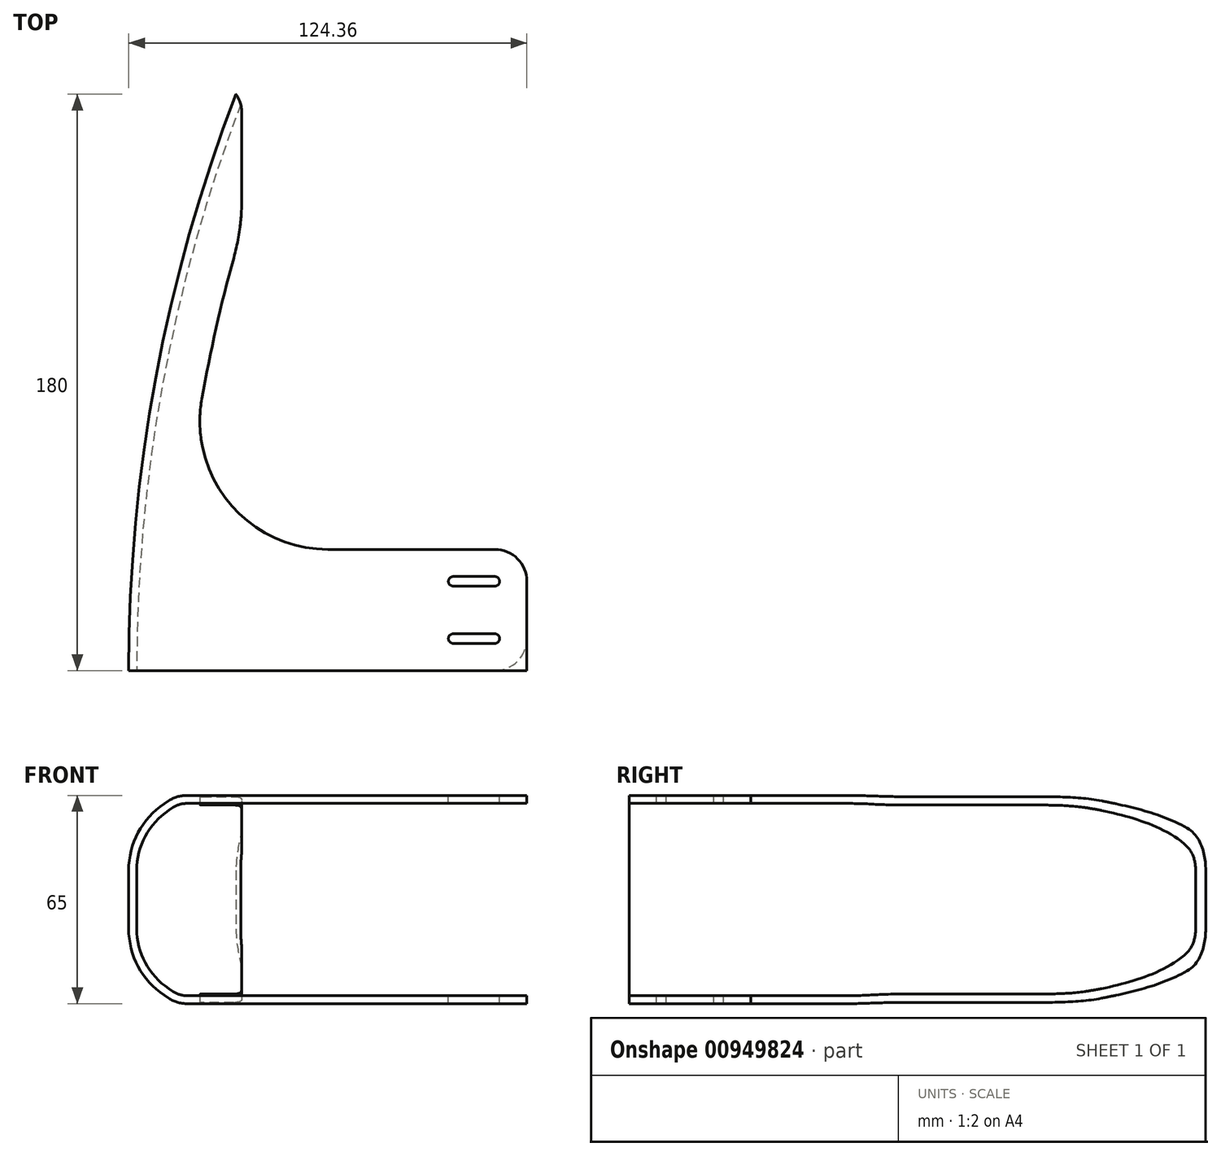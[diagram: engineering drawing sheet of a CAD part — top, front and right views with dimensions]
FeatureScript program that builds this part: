
annotation { "Feature Type Name" : "Feature", "Feature Type Description" : "" }
export const myFeature = defineFeature(function(context is Context, id is Id, definition is map)
    precondition{}
    {
        {
            var Q0;
            Q0=qCreatedBy(makeId("Top.planeOp"),FACE);
            var sketch = newSketch(context, id + "F0", { "sketchPlane" : qUnion([Q0])});
            skArc(sketch, "E0", {"start": v(-500, 0) * mm, "mid": v(-491.55, 91.55) * mm, "end": v(-466.48, 180) * mm});
            skLineSegment(sketch, "E1", {"start": v(-466.48, 180) * mm, "end": v(0, 0) * mm});
            skLineSegment(sketch, "E2", {"start": v(-500, 0) * mm, "end": v(0, 0) * mm});
            skSolve(sketch);
        }
        {
            var Q0;
            Q0=qSketchRegion(id+"F0",true);
            extrude(context, id + "F1", {"entities" : qUnion([Q0]), "depth" : 65 * mm, "offsetDistance" : 25 * mm});
        }
        {
            var Q0;
            Q0=makeQuery(id+"F1.opExtrude","CAP_EDGE",EDGE,{"disambiguationData":[OSD([sQuery(id+"F0.wireOp",EDGE,"E0")])],"isStart":true});
            var Q1;
            Q1=makeQuery(id+"F1.opExtrude","CAP_EDGE",EDGE,{"disambiguationData":[OSD([sQuery(id+"F0.wireOp",EDGE,"E0")])],"isStart":false});
            chamfer(context, id + "F2", {"entities" : qUnion([Q0, Q1]), "chamferType" : ChamferType.TWO_OFFSETS, "width1" : 10 * mm, "oppositeDirection" : false, "width2" : 15 * mm, "tangentPropagation" : true});
        }
        {
            var Q0;
            {var subQ0=sQuery(id+"F0.wireOp",EDGE,"E0");Q0=makeQuery(id+"F2.opChamfer","BLEND_EDGE",EDGE,{"blendedFrom":[makeQuery(id+"F1.opExtrude","CAP_EDGE",EDGE,{"disambiguationData":[OSD([subQ0])],"isStart":false}),makeQuery(id+"F1.opExtrude","SWEPT_FACE",FACE,{"disambiguationData":[OSD([subQ0])]})],"blendedInto":[makeQuery(id+"F1.opExtrude","SWEPT_FACE",FACE,{"disambiguationData":[OSD([subQ0])]})]});}
            var Q1;
            {var subQ0=sQuery(id+"F0.wireOp",EDGE,"E0");Q1=makeQuery(id+"F2.opChamfer","BLEND_EDGE",EDGE,{"blendedFrom":[makeQuery(id+"F1.opExtrude","CAP_EDGE",EDGE,{"disambiguationData":[OSD([subQ0])],"isStart":true}),makeQuery(id+"F1.opExtrude","SWEPT_FACE",FACE,{"disambiguationData":[OSD([subQ0])]})],"blendedInto":[makeQuery(id+"F1.opExtrude","SWEPT_FACE",FACE,{"disambiguationData":[OSD([subQ0])]})]});}
            fillet(context, id + "F3", {"entities" : qUnion([Q0, Q1]), "radius" : 25 * mm, "tangentPropagation" : true, "allowEdgeOverflow" : false});
        }
        {
            var Q0;
            {var subQ0=sQuery(id+"F0.wireOp",EDGE,"E0");Q0=makeQuery(id+"F2.opChamfer","BLEND_EDGE",EDGE,{"blendedFrom":[makeQuery(id+"F1.opExtrude","CAP_EDGE",EDGE,{"disambiguationData":[OSD([subQ0])],"isStart":false}),makeQuery(id+"F1.opExtrude","CAP_FACE",FACE,{"disambiguationData":[OSD([subQ0,sQuery(id+"F0.wireOp",EDGE,"E1"),sQuery(id+"F0.wireOp",EDGE,"E2")])],"isStart":false})],"blendedInto":[makeQuery(id+"F1.opExtrude","CAP_FACE",FACE,{"disambiguationData":[OSD([subQ0,sQuery(id+"F0.wireOp",EDGE,"E1"),sQuery(id+"F0.wireOp",EDGE,"E2")])],"isStart":false})]});}
            var Q1;
            {var subQ0=sQuery(id+"F0.wireOp",EDGE,"E0");Q1=makeQuery(id+"F2.opChamfer","BLEND_EDGE",EDGE,{"blendedFrom":[makeQuery(id+"F1.opExtrude","CAP_EDGE",EDGE,{"disambiguationData":[OSD([subQ0])],"isStart":true}),makeQuery(id+"F1.opExtrude","CAP_FACE",FACE,{"disambiguationData":[OSD([subQ0,sQuery(id+"F0.wireOp",EDGE,"E1"),sQuery(id+"F0.wireOp",EDGE,"E2")])],"isStart":true})],"blendedInto":[makeQuery(id+"F1.opExtrude","CAP_FACE",FACE,{"disambiguationData":[OSD([subQ0,sQuery(id+"F0.wireOp",EDGE,"E1"),sQuery(id+"F0.wireOp",EDGE,"E2")])],"isStart":true})]});}
            fillet(context, id + "F4", {"entities" : qUnion([Q0, Q1]), "radius" : 10 * mm, "tangentPropagation" : true, "allowEdgeOverflow" : false});
        }
        {
            var Q0;
            Q0=makeQuery(id+"F1.opExtrude","CAP_FACE",FACE,{"disambiguationData":[OSD([sQuery(id+"F0.wireOp",EDGE,"E0"),sQuery(id+"F0.wireOp",EDGE,"E1"),sQuery(id+"F0.wireOp",EDGE,"E2")])],"isStart":true});
            var sketch = newSketch(context, id + "F5", { "sketchPlane" : qUnion([Q0])});
            skLineSegment(sketch, "E3", {"start": v(-375.64, 0) * mm, "end": v(-375.64, -37.87) * mm});
            skLineSegment(sketch, "E4", {"start": v(-375.64, -37.87) * mm, "end": v(-445.64, -37.87) * mm});
            skLineSegment(sketch, "E5", {"start": v(-375.64, 0) * mm, "end": v(0, 0) * mm});
            skLineSegment(sketch, "E6", {"start": v(0, 0) * mm, "end": v(-452.15, -174.47) * mm});
            skArc(sketch, "E7", {"start": v(-480.57, -62.77) * mm, "mid": v(-469.7, -119.47) * mm, "end": v(-452.15, -174.47) * mm});
            skLineSegment(sketch, "E8", {"start": v(-452.15, -174.47) * mm, "end": v(0, 0) * mm});
            skArc(sketch, "E9", {"start": v(-480.57, -62.77) * mm, "mid": v(-482.03, -50.34) * mm, "end": v(-483.17, -37.87) * mm});
            skLineSegment(sketch, "E10", {"start": v(-445.64, -37.87) * mm, "end": v(-483.17, -37.87) * mm});
            skSolve(sketch);
        }
        {
            var Q0;
            Q0=qSketchRegion(id+"F5",true);
            extrude(context, id + "F6", {"entities" : qUnion([Q0]), "operationType" : NewBodyOperationType.REMOVE, "oppositeDirection" : true, "depth" : 100 * mm, "offsetDistance" : 25 * mm});
        }
        {
            var Q0;
            Q0=makeQuery(id+"F6.boolean.opBoolean","COPY",FACE,{"derivedFrom":makeQuery(id+"F6.opExtrude","SWEPT_FACE",FACE,{"disambiguationData":[OSD([sQuery(id+"F5.wireOp",EDGE,"q5jWbjDx-kVAx-P1jz-1uz1-IYKBsqEQwRC3")])]})});
            var Q1;
            Q1=makeQuery(id+"F6.boolean.opBoolean","COPY",FACE,{"derivedFrom":makeQuery(id+"F6.opExtrude","SWEPT_FACE",FACE,{"disambiguationData":[OSD([sQuery(id+"F5.wireOp",EDGE,"E4")])]})});
            var Q2;
            Q2=makeQuery(id+"F6.boolean.opBoolean","COPY",FACE,{"derivedFrom":makeQuery(id+"F6.opExtrude","SWEPT_FACE",FACE,{"disambiguationData":[OSD([sQuery(id+"F5.wireOp",EDGE,"2JUCW0xm-JYR1-ufkW-KHsm-7LWGHGezyxtH")])]})});
            var Q3;
            Q3=makeQuery(id+"F6.boolean.opBoolean","COPY",FACE,{"derivedFrom":makeQuery(id+"F6.opExtrude","SWEPT_FACE",FACE,{"disambiguationData":[OSD([sQuery(id+"F5.wireOp",EDGE,"E3")])]})});
            var Q4;
            Q4=makeQuery(id+"F6.boolean.opBoolean","COPY",FACE,{"derivedFrom":makeQuery(id+"F6.opExtrude","SWEPT_FACE",FACE,{"disambiguationData":[OSD([sQuery(id+"F5.wireOp",EDGE,"E7")])]})});
            var Q5;
            Q5=makeQuery(id+"F1.opExtrude","SWEPT_FACE",FACE,{"disambiguationData":[OSD([sQuery(id+"F0.wireOp",EDGE,"E1")])]});
            var Q6;
            Q6=makeQuery(id+"F1.opExtrude","SWEPT_FACE",FACE,{"disambiguationData":[OSD([sQuery(id+"F0.wireOp",EDGE,"E2")])]});
            shell(context, id + "F7", {"entities" : qUnion([Q0, Q1, Q2, Q3, Q4, Q5, Q6]), "thickness" : 2.5 * mm});
        }
        {
            var Q0;
            Q0=makeQuery(id+"F7.opShell","OFFSET_EDGE",EDGE,{"disambiguationData":[OSD([sQuery(id+"F5.wireOp",EDGE,"E3"),sQuery(id+"F5.wireOp",EDGE,"E4")])]});
            var Q1;
            Q1=makeQuery(id+"F7.opShell","OFFSET_EDGE",EDGE,{"disambiguationData":[OSD([sQuery(id+"F0.wireOp",EDGE,"E2"),sQuery(id+"F5.wireOp",EDGE,"E3"),sQuery(id+"F5.wireOp",EDGE,"E5")])]});
            var Q2;
            Q2=makeQuery(id+"F6.boolean.opBoolean","COPY",EDGE,{"derivedFrom":makeQuery(id+"F6.opExtrude","SWEPT_EDGE",EDGE,{"disambiguationData":[OSD([sQuery(id+"F5.wireOp",EDGE,"E3"),sQuery(id+"F5.wireOp",EDGE,"E4")])]})});
            var Q3;
            Q3=makeQuery(id+"F6.boolean.opBoolean","COPY",EDGE,{"derivedFrom":makeQuery(id+"F6.opExtrude","SWEPT_EDGE",EDGE,{"disambiguationData":[OSD([sQuery(id+"F0.wireOp",EDGE,"E2"),sQuery(id+"F5.wireOp",EDGE,"E3"),sQuery(id+"F5.wireOp",EDGE,"E5")])]})});
            fillet(context, id + "F8", {"entities" : qUnion([Q0, Q1, Q2, Q3]), "radius" : 10 * mm, "tangentPropagation" : true, "allowEdgeOverflow" : false});
        }
        {
            var Q0;
            Q0=makeQuery(id+"F1.opExtrude","CAP_FACE",FACE,{"disambiguationData":[OSD([sQuery(id+"F0.wireOp",EDGE,"E0"),sQuery(id+"F0.wireOp",EDGE,"E1"),sQuery(id+"F0.wireOp",EDGE,"E2")])],"isStart":false});
            var sketch = newSketch(context, id + "F9", { "sketchPlane" : qUnion([Q0])});
            skCircle(sketch, "E11", {"center": v(-385.64, 27.87) * mm, "radius": 1.5 * mm});
            skCircle(sketch, "E12", {"center": v(-385.64, 10) * mm, "radius": 1.5 * mm});
            skCircle(sketch, "E13", {"center": v(-398.64, 10) * mm, "radius": 1.5 * mm});
            skCircle(sketch, "E14", {"center": v(-398.64, 27.87) * mm, "radius": 1.5 * mm});
            skLineSegment(sketch, "E15", {"start": v(-398.64, 11.5) * mm, "end": v(-385.64, 11.5) * mm});
            skLineSegment(sketch, "E16", {"start": v(-398.64, 26.37) * mm, "end": v(-385.64, 26.37) * mm});
            skLineSegment(sketch, "E17", {"start": v(-385.64, 29.37) * mm, "end": v(-398.64, 29.37) * mm});
            skLineSegment(sketch, "E18", {"start": v(-398.64, 8.5) * mm, "end": v(-385.64, 8.5) * mm});
            skSolve(sketch);
        }
        {
            var Q0;
            Q0=qSketchRegion(id+"F9",true);
            extrude(context, id + "F10", {"entities" : qUnion([Q0]), "operationType" : NewBodyOperationType.REMOVE, "oppositeDirection" : true, "depth" : 500 * mm, "offsetDistance" : 25 * mm});
        }
        {
            var Q0;
            Q0=makeQuery(id+"F6.boolean.opBoolean","COPY",EDGE,{"derivedFrom":makeQuery(id+"F6.opExtrude","SWEPT_EDGE",EDGE,{"disambiguationData":[OSD([sQuery(id+"F5.wireOp",EDGE,"E9"),sQuery(id+"F5.wireOp",EDGE,"E10")])]})});
            var Q1;
            Q1=makeQuery(id+"F7.opShell","OFFSET_EDGE",EDGE,{"disambiguationData":[OSD([sQuery(id+"F5.wireOp",EDGE,"E9"),sQuery(id+"F5.wireOp",EDGE,"E10")])]});
            fillet(context, id + "F11", {"entities" : qUnion([Q0, Q1]), "radius" : 40 * mm, "tangentPropagation" : true, "allowEdgeOverflow" : false});
        }
        {
            var Q0;
            Q0=makeQuery(id+"F7.opShell","OFFSET_EDGE",EDGE,{"disambiguationData":[OSD([sQuery(id+"F5.wireOp",EDGE,"E7"),sQuery(id+"F5.wireOp",EDGE,"E8")])]});
            var Q1;
            Q1=makeQuery(id+"F6.boolean.opBoolean","COPY",EDGE,{"derivedFrom":makeQuery(id+"F6.opExtrude","SWEPT_EDGE",EDGE,{"disambiguationData":[OSD([sQuery(id+"F5.wireOp",EDGE,"E7"),sQuery(id+"F5.wireOp",EDGE,"E8")])]})});
            chamfer(context, id + "F12", {"entities" : qUnion([Q0, Q1]), "chamferType" : ChamferType.TWO_OFFSETS, "width1" : 15 * mm, "oppositeDirection" : false, "width2" : 40 * mm, "tangentPropagation" : true});
        }
        {
            var Q0;
            Q0=makeQuery(id+"F12.opChamfer","BLEND_EDGE",EDGE,{"blendedFrom":[makeQuery(id+"F7.opShell","OFFSET_EDGE",EDGE,{"disambiguationData":[OSD([sQuery(id+"F5.wireOp",EDGE,"E7"),sQuery(id+"F5.wireOp",EDGE,"E8")])]}),makeQuery(id+"F1.opExtrude","SWEPT_FACE",FACE,{"disambiguationData":[OSD([sQuery(id+"F0.wireOp",EDGE,"E1")])]})],"blendedInto":[makeQuery(id+"F1.opExtrude","SWEPT_FACE",FACE,{"disambiguationData":[OSD([sQuery(id+"F0.wireOp",EDGE,"E1")])]})]});
            fillet(context, id + "F13", {"entities" : qUnion([Q0]), "radius" : 10 * mm, "tangentPropagation" : true, "allowEdgeOverflow" : false});
        }
        {
            var Q0;
            {var subQ0=sQuery(id+"F5.wireOp",EDGE,"E7");Q0=makeQuery(id+"F12.opChamfer","BLEND_EDGE",EDGE,{"blendedFrom":[makeQuery(id+"F6.boolean.opBoolean","COPY",EDGE,{"derivedFrom":makeQuery(id+"F6.opExtrude","SWEPT_EDGE",EDGE,{"disambiguationData":[OSD([subQ0,sQuery(id+"F5.wireOp",EDGE,"E8")])]})}),makeQuery(id+"F7.opShell","OFFSET_FACE",FACE,{"disambiguationData":[OSD([subQ0,sQuery(id+"F5.wireOp",EDGE,"E9")])]})],"blendedInto":[makeQuery(id+"F7.opShell","OFFSET_FACE",FACE,{"disambiguationData":[OSD([subQ0,sQuery(id+"F5.wireOp",EDGE,"E9")])]})]});}
            var Q1;
            {var subQ0=sQuery(id+"F5.wireOp",EDGE,"E7");Q1=makeQuery(id+"F12.opChamfer","BLEND_EDGE",EDGE,{"blendedFrom":[makeQuery(id+"F7.opShell","OFFSET_EDGE",EDGE,{"disambiguationData":[OSD([subQ0,sQuery(id+"F5.wireOp",EDGE,"E8")])]}),makeQuery(id+"F6.boolean.opBoolean","COPY",FACE,{"derivedFrom":makeQuery(id+"F6.opExtrude","SWEPT_FACE",FACE,{"disambiguationData":[OSD([subQ0,sQuery(id+"F5.wireOp",EDGE,"E9")])]})})],"blendedInto":[makeQuery(id+"F6.boolean.opBoolean","COPY",FACE,{"derivedFrom":makeQuery(id+"F6.opExtrude","SWEPT_FACE",FACE,{"disambiguationData":[OSD([subQ0,sQuery(id+"F5.wireOp",EDGE,"E9")])]})})]});}
            var Q2;
            {var subQ0=sQuery(id+"F5.wireOp",EDGE,"E7");Q2=makeQuery(id+"F12.opChamfer","BLEND_EDGE",EDGE,{"blendedFrom":[makeQuery(id+"F7.opShell","OFFSET_EDGE",EDGE,{"disambiguationData":[OSD([subQ0,sQuery(id+"F5.wireOp",EDGE,"E8")])]}),makeQuery(id+"F7.opShell","OFFSET_FACE",FACE,{"disambiguationData":[OSD([subQ0,sQuery(id+"F5.wireOp",EDGE,"E9")])]})],"blendedInto":[makeQuery(id+"F7.opShell","OFFSET_FACE",FACE,{"disambiguationData":[OSD([subQ0,sQuery(id+"F5.wireOp",EDGE,"E9")])]})]});}
            fillet(context, id + "F14", {"entities" : qUnion([Q0, Q1, Q2]), "radius" : 70 * mm, "tangentPropagation" : true, "allowEdgeOverflow" : false});
        }
    });
